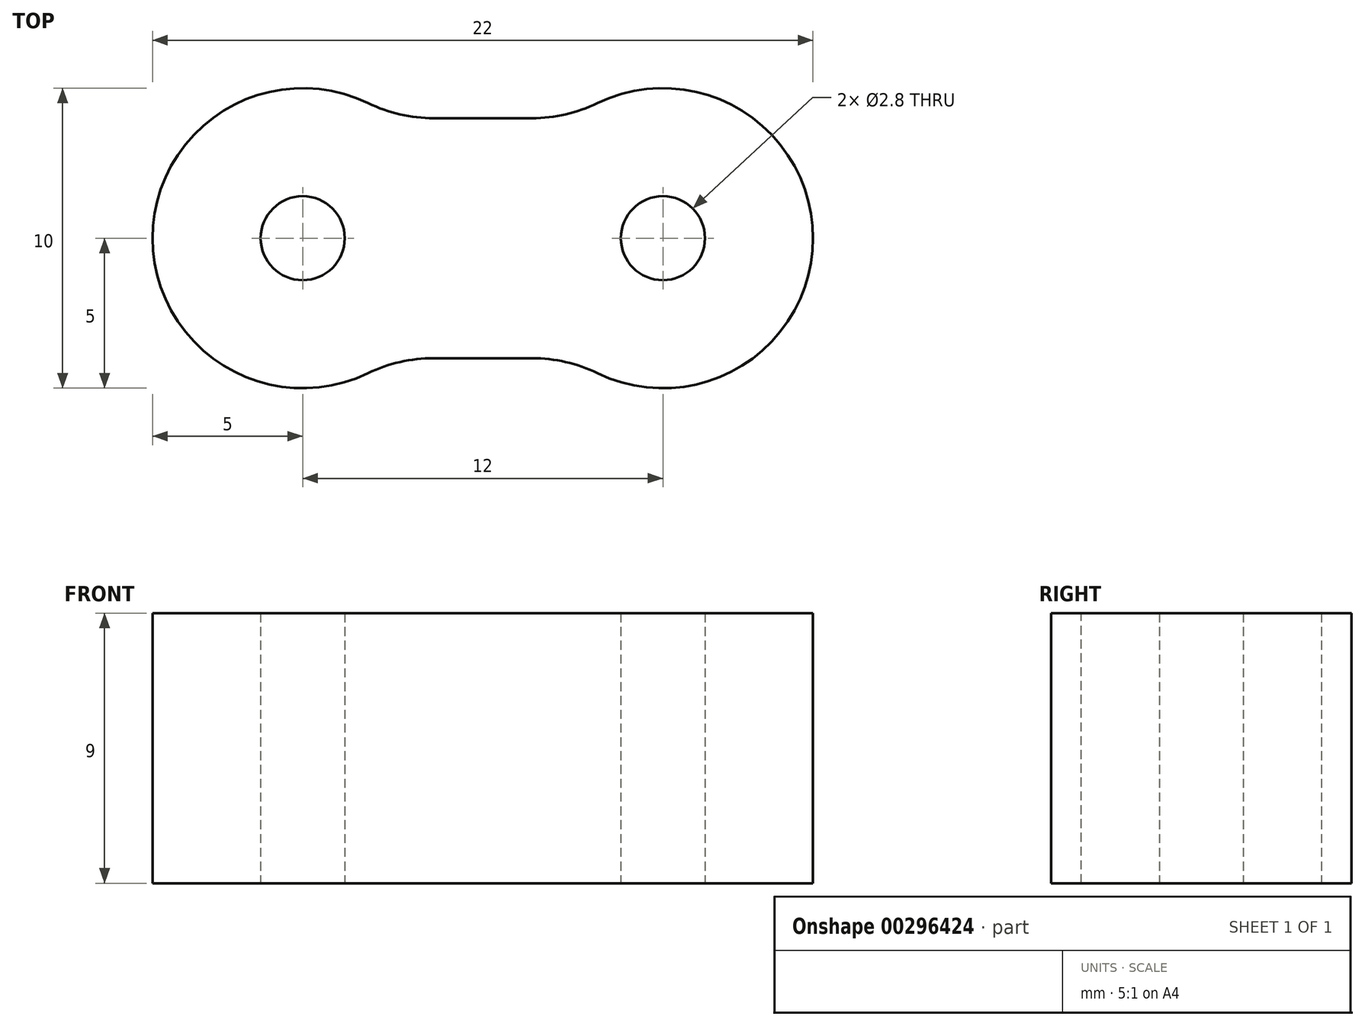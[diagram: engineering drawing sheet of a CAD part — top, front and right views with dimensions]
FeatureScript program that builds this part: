
annotation { "Feature Type Name" : "Feature", "Feature Type Description" : "" }
export const myFeature = defineFeature(function(context is Context, id is Id, definition is map)
    precondition{}
    {
        {
            var Q0;
            Q0=qCreatedBy(makeId("Top.planeOp"),FACE);
            var sketch = newSketch(context, id + "F0", { "sketchPlane" : qUnion([Q0])});
            skLineSegment(sketch, "E0", {"start": v(0, 0) * mm, "end": v(-6, 0) * mm});
            skCircle(sketch, "E1", {"center": v(-6, 0) * mm, "radius": 1.4 * mm});
            skCircle(sketch, "E2", {"center": v(-6, 0) * mm, "radius": 5 * mm});
            skLineSegment(sketch, "E3", {"start": v(-3, 4) * mm, "end": v(0, 4) * mm});
            skLineSegment(sketch, "E4.MirrorCS", {"start": v(-3, -4) * mm, "end": v(0, -4) * mm});
            skLineSegment(sketch, "E5", {"start": v(0, 4) * mm, "end": v(0, -4) * mm});
            skSolve(sketch);
        }
        {
            var Q0;
            Q0 = qSketchRegion(id + "F0", true);
            extrude(context, id + "F1", {"entities" : qUnion([Q0]), "depth" : 9 * mm, "offsetDistance" : 25 * mm});
        }
        {
            var Q0;
            Q0=makeQuery(id+"F1.opExtrude","SWEPT_EDGE",EDGE,{"disambiguationData":[OSD([sQuery(id+"F0.wireOp",EDGE,"E2"),sQuery(id+"F0.wireOp",EDGE,"E3")])]});
            var Q1;
            Q1=makeQuery(id+"F1.opExtrude","SWEPT_EDGE",EDGE,{"disambiguationData":[OSD([sQuery(id+"F0.wireOp",EDGE,"E2"),sQuery(id+"F0.wireOp",EDGE,"E4.MirrorCS")])]});
            fillet(context, id + "F2", {"entities" : qUnion([Q0, Q1]), "radius" : 5 * mm, "tangentPropagation" : true, "allowEdgeOverflow" : false});
        }
        {
            var Q0;
            Q0=makeQuery(id+"F1.opExtrude","SWEPT_BODY",BODY,{"disambiguationData":[OSD([sQuery(id+"F0.wireOp",EDGE,"E1"),sQuery(id+"F0.wireOp",EDGE,"E2"),sQuery(id+"F0.wireOp",EDGE,"E3"),sQuery(id+"F0.wireOp",EDGE,"E4.MirrorCS"),sQuery(id+"F0.wireOp",EDGE,"E5")])]});
            var Q1;
            Q1=makeQuery(id+"F1.opExtrude","SWEPT_FACE",FACE,{"disambiguationData":[OSD([sQuery(id+"F0.wireOp",EDGE,"E5")])]});
            mirror(context, id + "F3", {"operationType" : NewBodyOperationType.ADD, "entities" : qUnion([Q0]), "mirrorPlane" : qUnion([Q1])});
        }
    });
